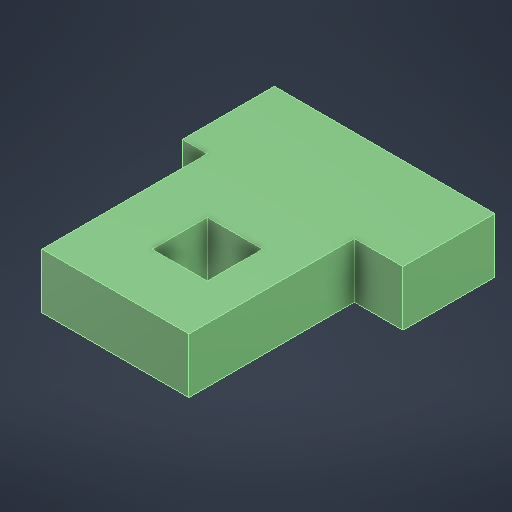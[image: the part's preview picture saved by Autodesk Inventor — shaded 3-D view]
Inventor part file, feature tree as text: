
AUTODESK INVENTOR PART (.ipt)
format: ipt  version: 2025.3 (Build 293356030, 356C)  size: 191,488 bytes
history: native  units: mm
features: other x1, extrude x1, sketch x1
ambient origin geometry x8: Origin, YZ Plane, XZ Plane, XY Plane, X Axis, Y Axis, Z Axis, Center Point
bodies: Body1 (feature_tree)
feature tree (3):
  other  "實體1"
  extrude  "擠出1"  Depth=8.0mm
  sketch  "草圖1"
